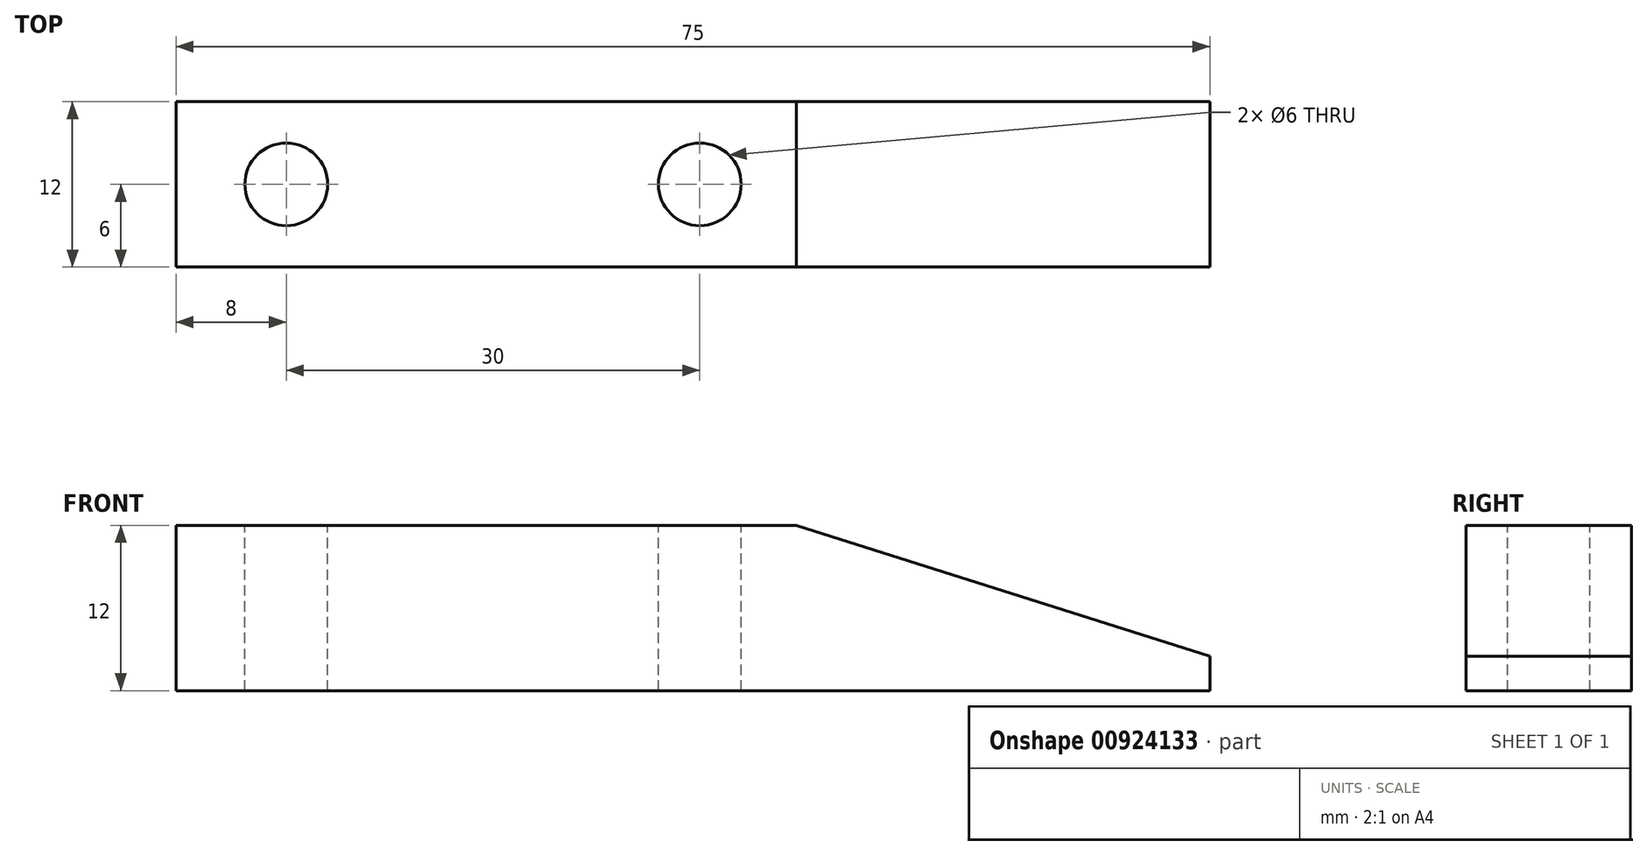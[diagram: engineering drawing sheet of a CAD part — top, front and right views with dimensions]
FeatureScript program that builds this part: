
annotation { "Feature Type Name" : "Feature", "Feature Type Description" : "" }
export const myFeature = defineFeature(function(context is Context, id is Id, definition is map)
    precondition{}
    {
        {
            var Q0;
            Q0=qCreatedBy(makeId("Front.planeOp"),FACE);
            var sketch = newSketch(context, id + "F0", { "sketchPlane" : qUnion([Q0])});
            skLineSegment(sketch, "E0", {"start": v(-30.7, -12) * mm, "end": v(44.3, -12) * mm});
            skLineSegment(sketch, "E1", {"start": v(44.3, -12) * mm, "end": v(44.3, -9.5) * mm});
            skLineSegment(sketch, "E2", {"start": v(14.3, 0) * mm, "end": v(-30.7, 0) * mm});
            skLineSegment(sketch, "E3", {"start": v(-30.7, 0) * mm, "end": v(-30.7, -12) * mm});
            skLineSegment(sketch, "E4", {"start": v(14.3, 0) * mm, "end": v(44.3, -9.5) * mm});
            skSolve(sketch);
        }
        {
            var Q0;
            Q0 = qSketchRegion(id + "F0", true);
            extrude(context, id + "F1", {"entities" : qUnion([Q0]), "depth" : 12 * mm, "offsetDistance" : 25 * mm});
        }
        {
            var Q0;
            Q0=makeQuery(id+"F1.opExtrude","SWEPT_FACE",FACE,{"disambiguationData":[OSD([sQuery(id+"F0.wireOp",EDGE,"E2")])]});
            var sketch = newSketch(context, id + "F2", { "sketchPlane" : qUnion([Q0])});
            skCircle(sketch, "E5", {"center": v(-22.7, -6) * mm, "radius": 3 * mm});
            skPoint(sketch, "E5.centerSnap0", {"position": v(-30.7, -6) * mm});
            skCircle(sketch, "E6", {"center": v(7.3, -6) * mm, "radius": 3 * mm});
            skSolve(sketch);
        }
        {
            var Q0;
            Q0 = qSketchRegion(id + "F2", true);
            extrude(context, id + "F3", {"entities" : qUnion([Q0]), "operationType" : NewBodyOperationType.REMOVE, "endBound" : BoundingType.THROUGH_ALL, "oppositeDirection" : true, "depth" : 25 * mm, "offsetDistance" : 25 * mm});
        }
    });
